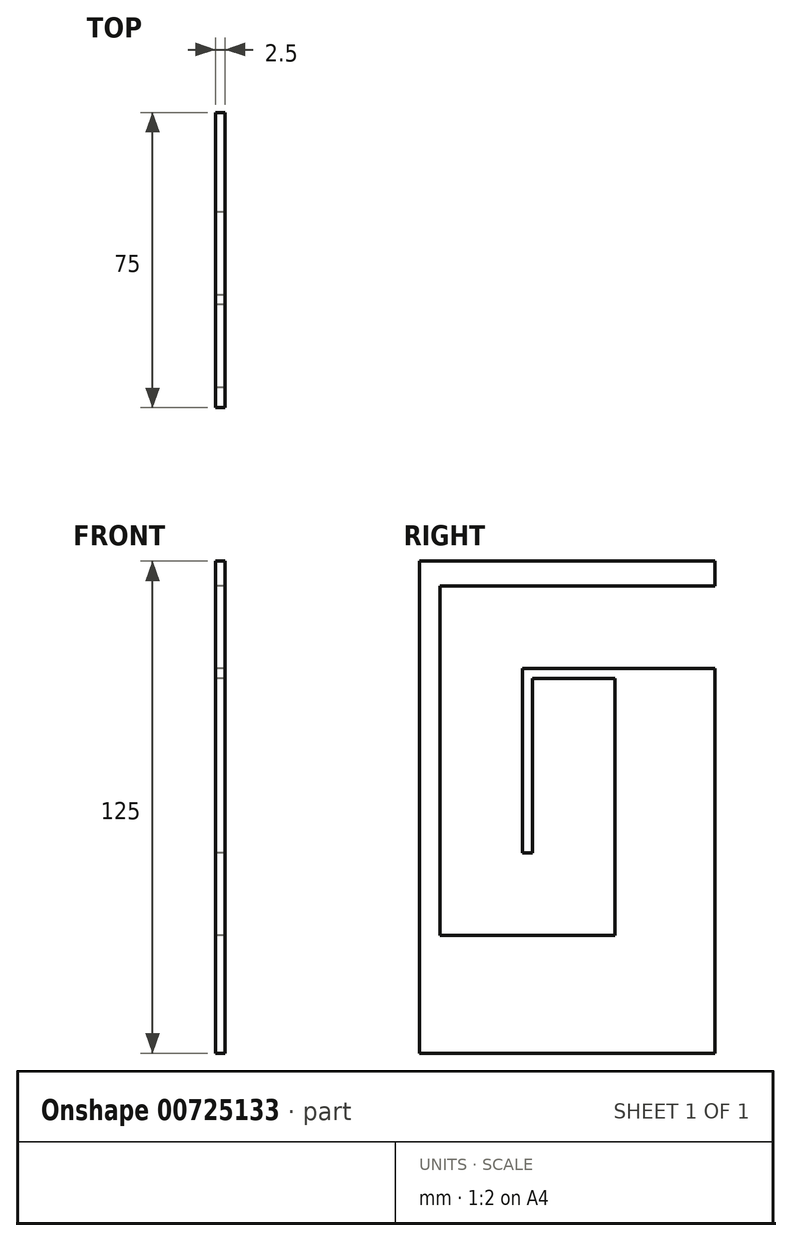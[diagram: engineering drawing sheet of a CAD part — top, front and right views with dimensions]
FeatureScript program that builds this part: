
annotation { "Feature Type Name" : "Feature", "Feature Type Description" : "" }
export const myFeature = defineFeature(function(context is Context, id is Id, definition is map)
    precondition{}
    {
        {
            var Q0;
            Q0=qCreatedBy(makeId("Right.planeOp"),FACE);
            var sketch = newSketch(context, id + "F0", { "sketchPlane" : qUnion([Q0])});
            skLineSegment(sketch, "E0.left", {"start": v(0, 0) * mm, "end": v(0, 125) * mm});
            skLineSegment(sketch, "E1.left", {"start": v(3.8, 121.19) * mm, "end": v(3.8, 3.8) * mm});
            skLineSegment(sketch, "E2", {"start": v(3.8, 121.19) * mm, "end": v(44.5, 121.19) * mm});
            skLineSegment(sketch, "E3", {"start": v(44.5, 121.19) * mm, "end": v(71.19, 121.19) * mm});
            skLineSegment(sketch, "E4", {"start": v(8.9, 3.81) * mm, "end": v(40.81, 3.81) * mm});
            skLineSegment(sketch, "E5", {"start": v(0, 0) * mm, "end": v(40.81, 0) * mm});
            skLineSegment(sketch, "E6", {"start": v(64.99, 0) * mm, "end": v(75, 0) * mm});
            skLineSegment(sketch, "E7", {"start": v(3.8, 3.8) * mm, "end": v(3.8, 0) * mm});
            skLineSegment(sketch, "E8", {"start": v(3.8, 0) * mm, "end": v(3.8, 3.8) * mm});
            skLineSegment(sketch, "E9", {"start": v(8.9, 3.81) * mm, "end": v(3.8, 3.8) * mm});
            skLineSegment(sketch, "E10", {"start": v(71.19, 3.81) * mm, "end": v(64.99, 3.81) * mm});
            skPoint(sketch, "E11.endSnap0", {"position": v(70, 0) * mm});
            skLineSegment(sketch, "E12", {"start": v(75, 125) * mm, "end": v(0, 125) * mm});
            skLineSegment(sketch, "E13", {"start": v(40.81, 3.81) * mm, "end": v(64.99, 3.81) * mm});
            skLineSegment(sketch, "E14", {"start": v(64.99, 0) * mm, "end": v(40.81, 0) * mm});
            skLineSegment(sketch, "E15", {"start": v(5.15, 29.89) * mm, "end": v(49.65, 29.9) * mm});
            skLineSegment(sketch, "E16", {"start": v(49.65, 29.9) * mm, "end": v(49.65, 71.46) * mm});
            skLineSegment(sketch, "E17", {"start": v(28.65, 71.46) * mm, "end": v(28.65, 95.25) * mm});
            skLineSegment(sketch, "E18", {"start": v(5.15, 8.89) * mm, "end": v(5.15, 29.9) * mm});
            skLineSegment(sketch, "E19", {"start": v(49.65, 29.9) * mm, "end": v(5.15, 29.89) * mm});
            skLineSegment(sketch, "E20", {"start": v(28.65, 71.46) * mm, "end": v(28.65, 50.9) * mm});
            skLineSegment(sketch, "E21", {"start": v(28.65, 50.9) * mm, "end": v(26.15, 50.9) * mm});
            skLineSegment(sketch, "E22", {"start": v(26.15, 50.9) * mm, "end": v(26.15, 95.25) * mm});
            skLineSegment(sketch, "E23", {"start": v(26.15, 95.25) * mm, "end": v(28.65, 95.25) * mm});
            skLineSegment(sketch, "E24", {"start": v(5.15, 29.9) * mm, "end": v(5.15, 118.75) * mm});
            skLineSegment(sketch, "E25", {"start": v(5.15, 118.75) * mm, "end": v(75, 118.75) * mm});
            skLineSegment(sketch, "E26", {"start": v(75, 97.75) * mm, "end": v(26.15, 97.75) * mm});
            skLineSegment(sketch, "E27", {"start": v(26.15, 97.75) * mm, "end": v(26.15, 95.25) * mm});
            skLineSegment(sketch, "E28", {"start": v(49.65, 71.46) * mm, "end": v(49.65, 95.25) * mm});
            skLineSegment(sketch, "E29", {"start": v(75, 118.75) * mm, "end": v(75, 125) * mm});
            skLineSegment(sketch, "E30", {"start": v(75, 97.75) * mm, "end": v(75, 0) * mm});
            skLineSegment(sketch, "E31", {"start": v(71.19, 125) * mm, "end": v(71.19, 118.75) * mm});
            skLineSegment(sketch, "E32", {"start": v(71.19, 97.75) * mm, "end": v(71.19, 0) * mm});
            skLineSegment(sketch, "E33", {"start": v(49.65, 95.25) * mm, "end": v(28.65, 95.25) * mm});
            skSolve(sketch);
        }
        {
            var Q0;
            Q0 = qSketchRegion(id + "F0", true);
            extrude(context, id + "F1", {"entities" : qUnion([Q0]), "depth" : 2.5 * mm, "offsetDistance" : 25.4 * mm});
        }
    });
